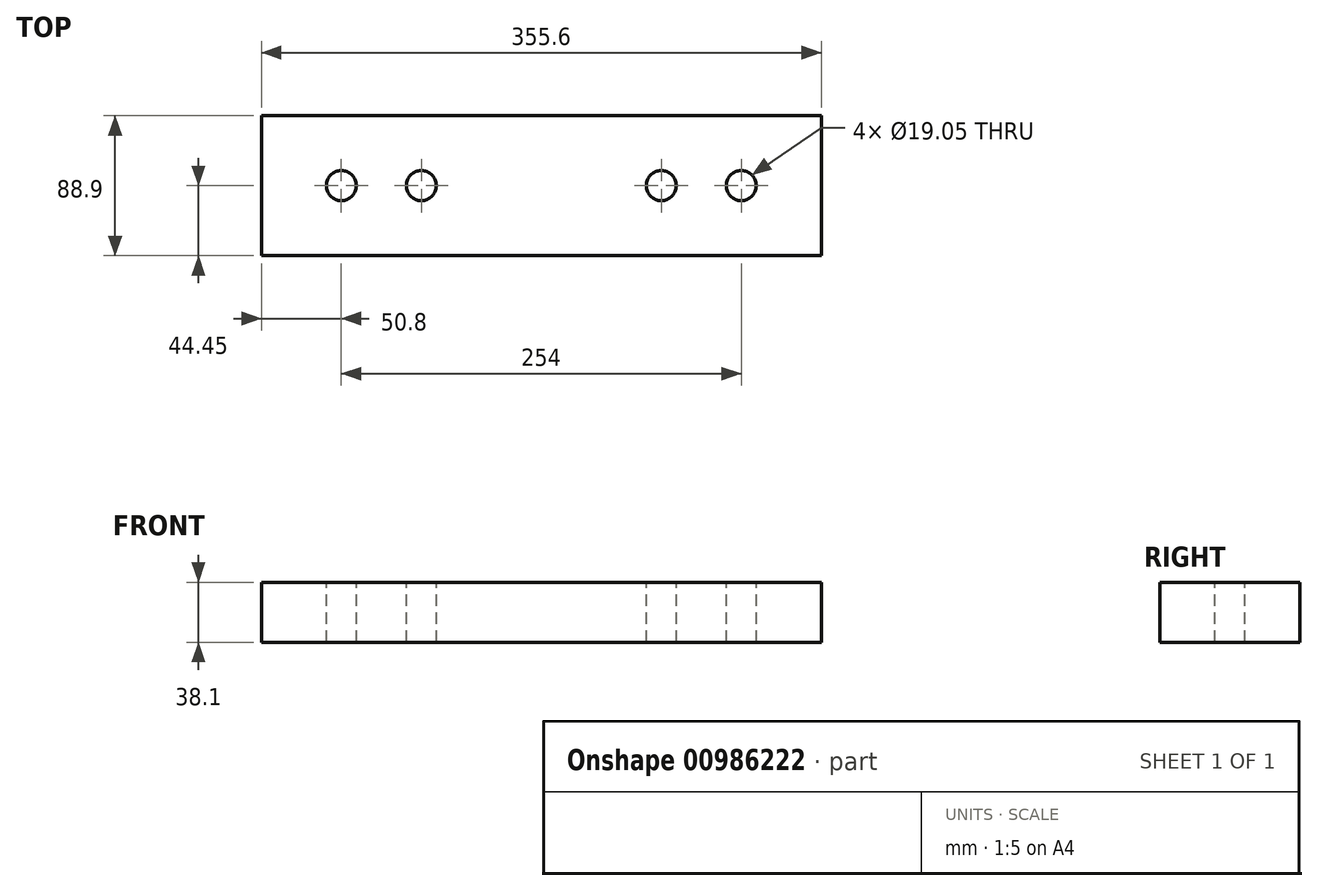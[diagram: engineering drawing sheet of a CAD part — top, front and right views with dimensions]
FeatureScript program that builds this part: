
annotation { "Feature Type Name" : "Feature", "Feature Type Description" : "" }
export const myFeature = defineFeature(function(context is Context, id is Id, definition is map)
    precondition{}
    {
        {
            var Q0;
            Q0=qCreatedBy(makeId("Right.planeOp"),FACE);
            var sketch = newSketch(context, id + "F0", { "sketchPlane" : qUnion([Q0])});
            skLineSegment(sketch, "E0.bottom", {"start": v(-44.45, 19.05) * mm, "end": v(44.45, 19.05) * mm});
            skLineSegment(sketch, "E0.top", {"start": v(-44.45, -19.05) * mm, "end": v(44.45, -19.05) * mm});
            skLineSegment(sketch, "E0.left", {"start": v(-44.45, 19.05) * mm, "end": v(-44.45, -19.05) * mm});
            skLineSegment(sketch, "E0.right", {"start": v(44.45, 19.05) * mm, "end": v(44.45, -19.05) * mm});
            skPoint(sketch, "E0.middle", {"position": v(0, 0) * mm});
            skSolve(sketch);
        }
        {
            var Q0;
            Q0=makeQuery(id+"F0.imprint","IMPRINT",FACE,{"disambiguationData":[TD([[makeQuery(id+"F0.imprint","IMPRINT",EDGE,{"derivedFrom":sQuery(id+"F0.wireOp",EDGE,"E0.bottom")}),-1.0]])]});
            extrude(context, id + "F1", {"entities" : qUnion([Q0]), "depth" : 355.6 * mm, "offsetDistance" : 25.4 * mm});
        }
        {
            var Q0;
            Q0=makeQuery(id+"F1.opExtrude","SWEPT_FACE",FACE,{"disambiguationData":[OSD([sQuery(id+"F0.wireOp",EDGE,"E0.bottom")])]});
            var sketch = newSketch(context, id + "F2", { "sketchPlane" : qUnion([Q0])});
            skCircle(sketch, "E1", {"center": v(50.8, 0) * mm, "radius": 9.53 * mm});
            skCircle(sketch, "E2", {"center": v(101.6, 0) * mm, "radius": 9.53 * mm});
            skCircle(sketch, "E3.1.0.0", {"center": v(254, 0) * mm, "radius": 9.53 * mm});
            skCircle(sketch, "E3.1.0.1", {"center": v(304.8, 0) * mm, "radius": 9.53 * mm});
            skLineSegment(sketch, "E3.direction1", {"start": v(50.8, 0) * mm, "end": v(254, 0) * mm, "construction": true});
            skSolve(sketch);
        }
        {
            var Q0;
            Q0=makeQuery(id+"F2.imprint","IMPRINT",FACE,{"disambiguationData":[TD([[makeQuery(id+"F2.imprint","IMPRINT",EDGE,{"derivedFrom":sQuery(id+"F2.wireOp",EDGE,"E1")}),1.0]])]});
            var Q1;
            Q1=makeQuery(id+"F2.imprint","IMPRINT",FACE,{"disambiguationData":[TD([[makeQuery(id+"F2.imprint","IMPRINT",EDGE,{"derivedFrom":sQuery(id+"F2.wireOp",EDGE,"E2")}),1.0]])]});
            var Q2;
            Q2=makeQuery(id+"F2.imprint","IMPRINT",FACE,{"disambiguationData":[TD([[makeQuery(id+"F2.imprint","IMPRINT",EDGE,{"derivedFrom":sQuery(id+"F2.wireOp",EDGE,"E3.1.0.0")}),1.0]])]});
            var Q3;
            Q3=makeQuery(id+"F2.imprint","IMPRINT",FACE,{"disambiguationData":[TD([[makeQuery(id+"F2.imprint","IMPRINT",EDGE,{"derivedFrom":sQuery(id+"F2.wireOp",EDGE,"E3.1.0.1")}),1.0]])]});
            extrude(context, id + "F3", {"entities" : qUnion([Q0, Q1, Q2, Q3]), "operationType" : NewBodyOperationType.REMOVE, "endBound" : BoundingType.THROUGH_ALL, "oppositeDirection" : true, "depth" : 25.4 * mm, "offsetDistance" : 25.4 * mm});
        }
    });
